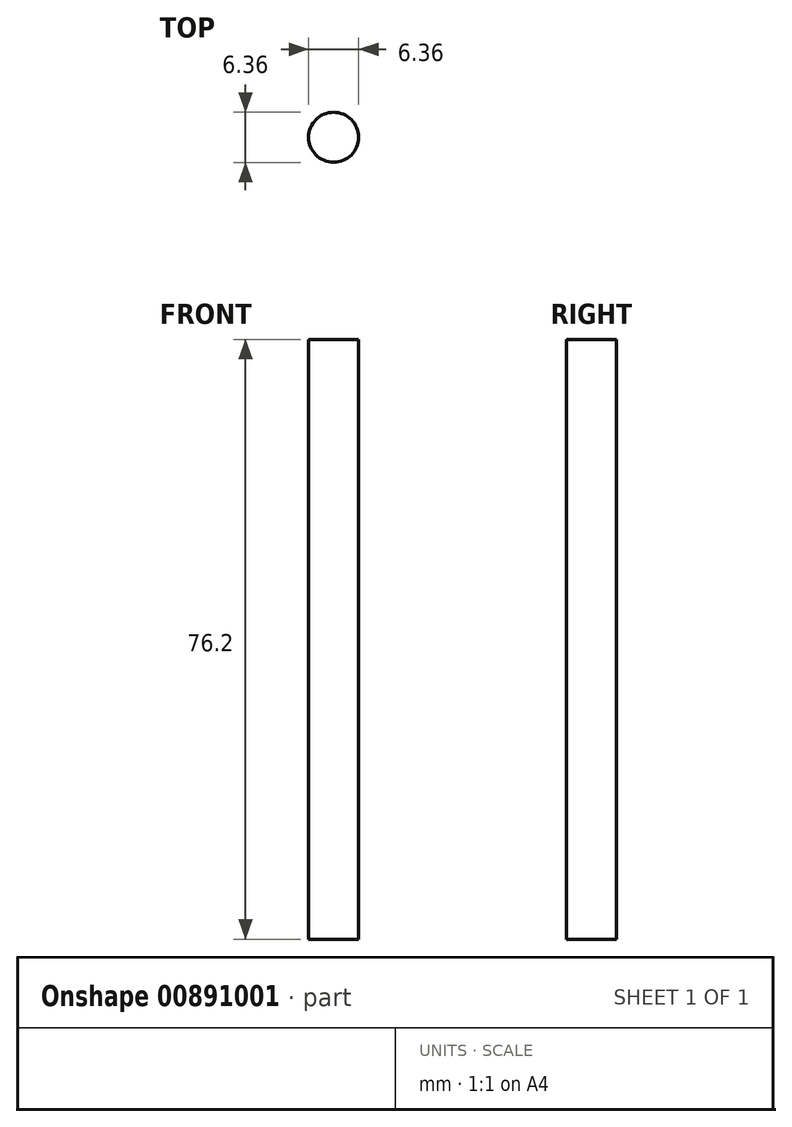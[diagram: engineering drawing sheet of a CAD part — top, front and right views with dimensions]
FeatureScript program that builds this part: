
annotation { "Feature Type Name" : "Feature", "Feature Type Description" : "" }
export const myFeature = defineFeature(function(context is Context, id is Id, definition is map)
    precondition{}
    {
        {
            var Q0;
            Q0=qCreatedBy(makeId("Top.planeOp"),FACE);
            var sketch = newSketch(context, id + "F0", { "sketchPlane" : qUnion([Q0])});
            skCircle(sketch, "E0", {"center": v(0, 0) * mm, "radius": 3.18 * mm});
            skSolve(sketch);
        }
        {
            var Q0;
            Q0 = qSketchRegion(id + "F0", true);
            extrude(context, id + "F1", {"entities" : qUnion([Q0]), "depth" : 76.2 * mm, "offsetDistance" : 25.4 * mm});
        }
    });
